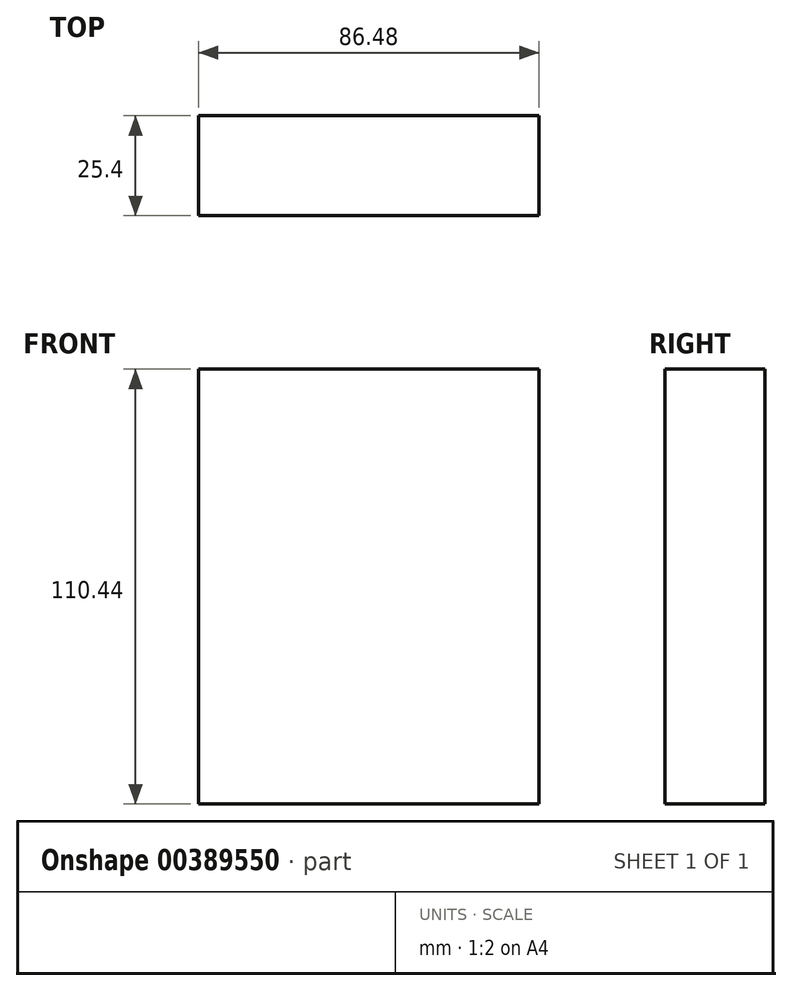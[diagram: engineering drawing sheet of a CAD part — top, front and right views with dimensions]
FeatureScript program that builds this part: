
annotation { "Feature Type Name" : "Feature", "Feature Type Description" : "" }
export const myFeature = defineFeature(function(context is Context, id is Id, definition is map)
    precondition{}
    {
        {
            var Q0;
            Q0=qCreatedBy(makeId("Front.planeOp"),FACE);
            var sketch = newSketch(context, id + "F0", { "sketchPlane" : qUnion([Q0])});
            skLineSegment(sketch, "E0.bottom", {"start": v(43.24, 55.22) * mm, "end": v(-43.24, 55.22) * mm});
            skLineSegment(sketch, "E0.top", {"start": v(43.24, -55.22) * mm, "end": v(-43.24, -55.22) * mm});
            skLineSegment(sketch, "E0.left", {"start": v(43.24, 55.22) * mm, "end": v(43.24, -55.22) * mm});
            skLineSegment(sketch, "E0.right", {"start": v(-43.24, 55.22) * mm, "end": v(-43.24, -55.22) * mm});
            skPoint(sketch, "E0.middle", {"position": v(0, 0) * mm});
            skSolve(sketch);
        }
        {
            var Q0;
            Q0 = qSketchRegion(id + "F0", true);
            extrude(context, id + "F1", {"entities" : qUnion([Q0]), "depth" : 25.4 * mm});
        }
    });
